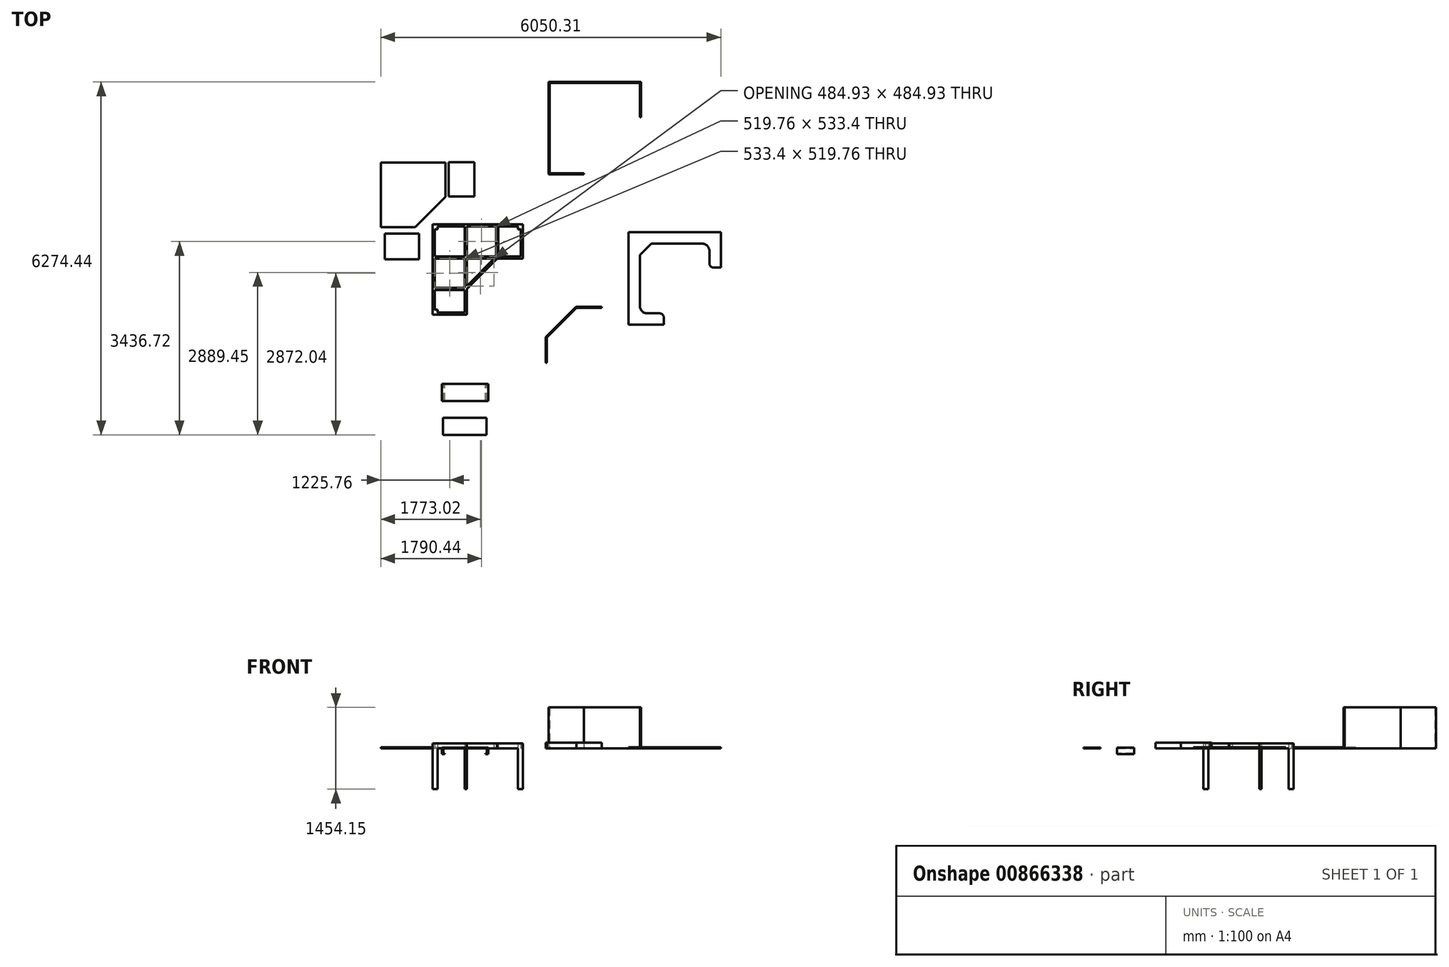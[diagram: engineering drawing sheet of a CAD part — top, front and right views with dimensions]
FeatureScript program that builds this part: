
annotation { "Feature Type Name" : "Feature", "Feature Type Description" : "" }
export const myFeature = defineFeature(function(context is Context, id is Id, definition is map)
    precondition{}
    {
        {
            var Q0;
            Q0=qCreatedBy(makeId("Top.planeOp"),FACE);
            var sketch = newSketch(context, id + "F0", { "sketchPlane" : qUnion([Q0])});
            skLineSegment(sketch, "E0.bottom", {"start": v(-1200.38, 871.33) * mm, "end": v(405.23, 871.33) * mm});
            skLineSegment(sketch, "E0.top", {"start": v(-1200.38, -734.28) * mm, "end": v(405.23, -734.28) * mm});
            skLineSegment(sketch, "E0.left", {"start": v(-1200.38, 871.33) * mm, "end": v(-1200.38, -734.28) * mm});
            skLineSegment(sketch, "E0.right", {"start": v(405.23, 871.33) * mm, "end": v(405.23, -734.28) * mm});
            skLineSegment(sketch, "E1.bottom", {"start": v(405.23, -734.28) * mm, "end": v(-590.78, -734.28) * mm});
            skLineSegment(sketch, "E1.top", {"start": v(405.23, 261.73) * mm, "end": v(-590.78, 261.73) * mm});
            skLineSegment(sketch, "E1.left", {"start": v(405.23, -734.28) * mm, "end": v(405.23, 261.73) * mm});
            skLineSegment(sketch, "E1.right", {"start": v(-590.78, -734.28) * mm, "end": v(-590.78, 261.73) * mm});
            skLineSegment(sketch, "E2", {"start": v(-590.78, -277.08) * mm, "end": v(-51.97, 261.73) * mm});
            skLineSegment(sketch, "E3", {"start": v(-590.78, -277.08) * mm, "end": v(-1200.38, -277.08) * mm});
            skLineSegment(sketch, "E4", {"start": v(-51.97, 261.73) * mm, "end": v(-51.97, 871.33) * mm});
            skLineSegment(sketch, "E5", {"start": v(-1200.38, -24.58) * mm, "end": v(-304.48, 871.33) * mm});
            skSolve(sketch);
        }
        {
            var Q0;
            {var subQ5=sQuery(id+"F0.wireOp",EDGE,"E3");Q0=makeQuery(id+"F0.imprint","IMPRINT",FACE,{"disambiguationData":[TD([[makeQuery(id+"F0.imprint","IMPRINT",EDGE,{"derivedFrom":subQ5}),-1.0]])]});}
            var Q1;
            {var subQ0=sQuery(id+"F0.wireOp",EDGE,"E2");Q1=makeQuery(id+"F0.imprint","IMPRINT",FACE,{"disambiguationData":[TD([[makeQuery(id+"F0.imprint","IMPRINT",EDGE,{"derivedFrom":subQ0}),1.0]])]});}
            var Q2;
            {var subQ3=sQuery(id+"F0.wireOp",EDGE,"E5");Q2=makeQuery(id+"F0.imprint","IMPRINT",FACE,{"disambiguationData":[TD([[makeQuery(id+"F0.imprint","IMPRINT",EDGE,{"derivedFrom":subQ3}),1.0]])]});}
            extrude(context, id + "F1", {"entities" : qUnion([Q0, Q1, Q2]), "depth" : 19.05 * mm, "offsetDistance" : 25.4 * mm});
        }
        {
            var Q0;
            Q0=qCreatedBy(makeId("Top.planeOp"),FACE);
            var sketch = newSketch(context, id + "F2", { "sketchPlane" : qUnion([Q0])});
            skLineSegment(sketch, "E6.bottom", {"start": v(-1128.15, -392.27) * mm, "end": v(-518.55, -392.27) * mm});
            skLineSegment(sketch, "E6.top", {"start": v(-1128.15, -849.47) * mm, "end": v(-518.55, -849.47) * mm});
            skLineSegment(sketch, "E6.left", {"start": v(-1128.15, -392.27) * mm, "end": v(-1128.15, -849.47) * mm});
            skLineSegment(sketch, "E6.right", {"start": v(-518.55, -392.27) * mm, "end": v(-518.55, -849.47) * mm});
            skLineSegment(sketch, "E7.bottom", {"start": v(3.93, 267.1) * mm, "end": v(461.13, 267.1) * mm});
            skLineSegment(sketch, "E7.top", {"start": v(3.93, 876.7) * mm, "end": v(461.13, 876.7) * mm});
            skLineSegment(sketch, "E7.left", {"start": v(3.93, 267.1) * mm, "end": v(3.93, 876.7) * mm});
            skLineSegment(sketch, "E7.right", {"start": v(461.13, 267.1) * mm, "end": v(461.13, 876.7) * mm});
            skSolve(sketch);
        }
        {
            var Q0;
            Q0=makeQuery(id+"F2.imprint","IMPRINT",FACE,{"disambiguationData":[TD([[makeQuery(id+"F2.imprint","IMPRINT",EDGE,{"derivedFrom":sQuery(id+"F2.wireOp",EDGE,"E6.bottom")}),-1.0]])]});
            var Q1;
            Q1=makeQuery(id+"F2.imprint","IMPRINT",FACE,{"disambiguationData":[TD([[makeQuery(id+"F2.imprint","IMPRINT",EDGE,{"derivedFrom":sQuery(id+"F2.wireOp",EDGE,"E7.bottom")}),1.0]])]});
            extrude(context, id + "F3", {"entities" : qUnion([Q0, Q1]), "depth" : 19.05 * mm, "offsetDistance" : 25.4 * mm});
        }
        {
            var Q0;
            Q0=qCreatedBy(makeId("Top.planeOp"),FACE);
            var sketch = newSketch(context, id + "F4", { "sketchPlane" : qUnion([Q0])});
            skLineSegment(sketch, "E8.bottom", {"start": v(-279.42, -229.72) * mm, "end": v(1326.19, -229.72) * mm});
            skLineSegment(sketch, "E8.top", {"start": v(-279.42, -1835.33) * mm, "end": v(1326.19, -1835.33) * mm});
            skLineSegment(sketch, "E8.left", {"start": v(-279.42, -229.72) * mm, "end": v(-279.42, -1835.33) * mm});
            skLineSegment(sketch, "E8.right", {"start": v(1326.19, -229.72) * mm, "end": v(1326.19, -1835.33) * mm});
            skLineSegment(sketch, "E9.bottom", {"start": v(1326.19, -1835.33) * mm, "end": v(330.18, -1835.33) * mm});
            skLineSegment(sketch, "E9.top", {"start": v(1326.19, -839.32) * mm, "end": v(330.18, -839.32) * mm});
            skLineSegment(sketch, "E9.left", {"start": v(1326.19, -1835.33) * mm, "end": v(1326.19, -839.32) * mm});
            skLineSegment(sketch, "E9.right", {"start": v(330.18, -1835.33) * mm, "end": v(330.18, -839.32) * mm});
            skLineSegment(sketch, "E10", {"start": v(330.18, -1378.13) * mm, "end": v(868.99, -839.32) * mm});
            skLineSegment(sketch, "E11.bottom", {"start": v(-279.42, -1746.43) * mm, "end": v(-241.32, -1746.43) * mm});
            skLineSegment(sketch, "E11.top", {"start": v(-279.42, -318.62) * mm, "end": v(-241.32, -318.62) * mm});
            skLineSegment(sketch, "E11.left", {"start": v(-279.42, -1746.43) * mm, "end": v(-279.42, -318.62) * mm});
            skLineSegment(sketch, "E11.right", {"start": v(-241.32, -1746.43) * mm, "end": v(-241.32, -318.62) * mm});
            skLineSegment(sketch, "E12.bottom", {"start": v(-190.52, -229.72) * mm, "end": v(1237.29, -229.72) * mm});
            skLineSegment(sketch, "E12.top", {"start": v(-190.52, -267.82) * mm, "end": v(1237.29, -267.82) * mm});
            skLineSegment(sketch, "E12.left", {"start": v(-190.52, -229.72) * mm, "end": v(-190.52, -267.82) * mm});
            skLineSegment(sketch, "E12.right", {"start": v(1237.29, -229.72) * mm, "end": v(1237.29, -267.82) * mm});
            skLineSegment(sketch, "E13.bottom", {"start": v(1326.19, -801.22) * mm, "end": v(1288.09, -801.22) * mm});
            skLineSegment(sketch, "E13.top", {"start": v(1326.19, -318.62) * mm, "end": v(1288.09, -318.62) * mm});
            skLineSegment(sketch, "E13.left", {"start": v(1326.19, -801.22) * mm, "end": v(1326.19, -318.62) * mm});
            skLineSegment(sketch, "E13.right", {"start": v(1288.09, -801.22) * mm, "end": v(1288.09, -318.62) * mm});
            skLineSegment(sketch, "E14.bottom", {"start": v(292.08, -1835.33) * mm, "end": v(-190.52, -1835.33) * mm});
            skLineSegment(sketch, "E14.top", {"start": v(292.08, -1797.23) * mm, "end": v(-190.52, -1797.23) * mm});
            skLineSegment(sketch, "E14.left", {"start": v(292.08, -1835.33) * mm, "end": v(292.08, -1797.23) * mm});
            skLineSegment(sketch, "E14.right", {"start": v(-190.52, -1835.33) * mm, "end": v(-190.52, -1797.23) * mm});
            skLineSegment(sketch, "E15.bottom", {"start": v(330.18, -1746.43) * mm, "end": v(292.08, -1746.43) * mm});
            skLineSegment(sketch, "E15.top", {"start": v(330.18, -267.82) * mm, "end": v(292.08, -267.82) * mm});
            skLineSegment(sketch, "E15.left", {"start": v(330.18, -1746.43) * mm, "end": v(330.18, -267.82) * mm});
            skLineSegment(sketch, "E15.right", {"start": v(292.08, -1746.43) * mm, "end": v(292.08, -267.82) * mm});
            skLineSegment(sketch, "E16.bottom", {"start": v(1237.29, -839.32) * mm, "end": v(-241.32, -839.32) * mm});
            skLineSegment(sketch, "E16.top", {"start": v(1237.29, -801.22) * mm, "end": v(-241.32, -801.22) * mm});
            skLineSegment(sketch, "E16.left", {"start": v(1237.29, -839.32) * mm, "end": v(1237.29, -801.22) * mm});
            skLineSegment(sketch, "E16.right", {"start": v(-241.32, -839.32) * mm, "end": v(-241.32, -801.22) * mm});
            skLineSegment(sketch, "E17.bottom", {"start": v(1326.19, -839.32) * mm, "end": v(1237.29, -839.32) * mm});
            skLineSegment(sketch, "E17.top", {"start": v(1326.19, -801.22) * mm, "end": v(1237.29, -801.22) * mm});
            skLineSegment(sketch, "E17.left", {"start": v(1326.19, -839.32) * mm, "end": v(1326.19, -801.22) * mm});
            skLineSegment(sketch, "E18.bottom", {"start": v(1326.19, -229.72) * mm, "end": v(1237.29, -229.72) * mm});
            skLineSegment(sketch, "E18.left", {"start": v(1326.19, -229.72) * mm, "end": v(1326.19, -318.61) * mm});
            skLineSegment(sketch, "E19.bottom", {"start": v(-279.42, -229.72) * mm, "end": v(-190.52, -229.72) * mm});
            skLineSegment(sketch, "E19.left", {"start": v(-279.42, -229.72) * mm, "end": v(-279.42, -318.61) * mm});
            skLineSegment(sketch, "E20.bottom", {"start": v(-279.42, -1835.33) * mm, "end": v(-190.52, -1835.33) * mm});
            skLineSegment(sketch, "E20.top", {"start": v(-279.42, -1746.43) * mm, "end": v(-190.52, -1746.43) * mm});
            skLineSegment(sketch, "E20.left", {"start": v(-279.42, -1835.33) * mm, "end": v(-279.42, -1746.43) * mm});
            skLineSegment(sketch, "E20.right", {"start": v(-190.52, -1835.33) * mm, "end": v(-190.52, -1746.43) * mm});
            skLineSegment(sketch, "E21.bottom", {"start": v(330.18, -1835.33) * mm, "end": v(292.08, -1835.33) * mm});
            skLineSegment(sketch, "E21.left", {"start": v(330.18, -1835.33) * mm, "end": v(330.18, -1746.43) * mm});
            skLineSegment(sketch, "E21.right", {"start": v(292.08, -1835.33) * mm, "end": v(292.08, -1746.43) * mm});
            skLineSegment(sketch, "E22", {"start": v(330.18, -1324.25) * mm, "end": v(815.1, -839.32) * mm});
            skLineSegment(sketch, "E23.bottom", {"start": v(888.04, -801.22) * mm, "end": v(849.94, -801.22) * mm});
            skLineSegment(sketch, "E23.top", {"start": v(888.04, -267.82) * mm, "end": v(849.94, -267.82) * mm});
            skLineSegment(sketch, "E23.left", {"start": v(888.04, -801.22) * mm, "end": v(888.04, -267.82) * mm});
            skLineSegment(sketch, "E23.right", {"start": v(849.94, -801.22) * mm, "end": v(849.94, -267.82) * mm});
            skLineSegment(sketch, "E24.bottom", {"start": v(292.08, -1397.18) * mm, "end": v(-241.32, -1397.18) * mm});
            skLineSegment(sketch, "E24.top", {"start": v(292.08, -1359.08) * mm, "end": v(-241.32, -1359.08) * mm});
            skLineSegment(sketch, "E24.left", {"start": v(292.08, -1397.18) * mm, "end": v(292.08, -1359.08) * mm});
            skLineSegment(sketch, "E24.right", {"start": v(-241.32, -1397.18) * mm, "end": v(-241.32, -1359.08) * mm});
            skLineSegment(sketch, "E25.top", {"start": v(1326.19, -318.62) * mm, "end": v(1237.29, -318.62) * mm});
            skLineSegment(sketch, "E25.left", {"start": v(1326.19, -229.72) * mm, "end": v(1326.19, -318.62) * mm});
            skLineSegment(sketch, "E25.right", {"start": v(1237.29, -229.72) * mm, "end": v(1237.29, -318.62) * mm});
            skLineSegment(sketch, "E26.top", {"start": v(-279.42, -318.62) * mm, "end": v(-190.52, -318.62) * mm});
            skLineSegment(sketch, "E26.left", {"start": v(-279.42, -229.72) * mm, "end": v(-279.42, -318.62) * mm});
            skLineSegment(sketch, "E26.right", {"start": v(-190.52, -229.72) * mm, "end": v(-190.52, -318.62) * mm});
            skSolve(sketch);
        }
        {
            var Q0;
            {var subQ6=sQuery(id+"F4.wireOp",EDGE,"E11.top");Q0=makeQuery(id+"F4.imprint","IMPRINT",FACE,{"disambiguationData":[TD([[makeQuery(id+"F4.imprint","IMPRINT",EDGE,{"derivedFrom":subQ6}),-1.0]])]});}
            var Q1;
            {var subQ1=sQuery(id+"F4.wireOp",EDGE,"E19.bottom");Q1=makeQuery(id+"F4.imprint","IMPRINT",FACE,{"disambiguationData":[TD([[makeQuery(id+"F4.imprint","IMPRINT",EDGE,{"derivedFrom":subQ1}),-1.0]])]});}
            var Q2;
            {var subQ3=sQuery(id+"F4.wireOp",EDGE,"E12.left");Q2=makeQuery(id+"F4.imprint","IMPRINT",FACE,{"disambiguationData":[TD([[makeQuery(id+"F4.imprint","IMPRINT",EDGE,{"derivedFrom":subQ3}),1.0]])]});}
            var Q3;
            {var subQ0=sQuery(id+"F4.wireOp",EDGE,"E15.left");var subQ1=sQuery(id+"F4.wireOp",EDGE,"E12.top");var subQ2=makeQuery(id+"F4.imprint","INTERSECT",VERTEX,{"derivedFrom":[subQ1,subQ0]});Q3=makeQuery(id+"F4.imprint","IMPRINT",FACE,{"disambiguationData":[TD([[makeQuery(id+"F4.imprint","IMPRINT",EDGE,{"disambiguationData":[TD([[subQ2,1.0]])],"derivedFrom":subQ1}),-1.0]])]});}
            var Q4;
            {var subQ0=sQuery(id+"F4.wireOp",EDGE,"E16.top");var subQ1=sQuery(id+"F4.wireOp",EDGE,"E11.right");var subQ2=makeQuery(id+"F4.imprint","INTERSECT",VERTEX,{"derivedFrom":[subQ1,subQ0]});Q4=makeQuery(id+"F4.imprint","IMPRINT",FACE,{"disambiguationData":[TD([[makeQuery(id+"F4.imprint","IMPRINT",EDGE,{"disambiguationData":[TD([[subQ2,1.0]])],"derivedFrom":subQ1}),-1.0]])]});}
            var Q5;
            {var subQ0=sQuery(id+"F4.wireOp",EDGE,"E16.top");var subQ5=sQuery(id+"F4.wireOp",EDGE,"E15.right");var subQ6=makeQuery(id+"F4.imprint","INTERSECT",VERTEX,{"derivedFrom":[subQ5,subQ0]});Q5=makeQuery(id+"F4.imprint","IMPRINT",FACE,{"disambiguationData":[TD([[makeQuery(id+"F4.imprint","IMPRINT",EDGE,{"disambiguationData":[TD([[subQ6,1.0]])],"derivedFrom":subQ5}),-1.0]])]});}
            var Q6;
            {var subQ3=sQuery(id+"F4.wireOp",EDGE,"E15.bottom");Q6=makeQuery(id+"F4.imprint","IMPRINT",FACE,{"disambiguationData":[TD([[makeQuery(id+"F4.imprint","IMPRINT",EDGE,{"derivedFrom":subQ3}),-1.0]])]});}
            var Q7;
            {var subQ7=sQuery(id+"F4.wireOp",EDGE,"E16.left");Q7=makeQuery(id+"F4.imprint","IMPRINT",FACE,{"disambiguationData":[TD([[makeQuery(id+"F4.imprint","IMPRINT",EDGE,{"derivedFrom":subQ7}),1.0]])]});}
            var Q8;
            {var subQ0=sQuery(id+"F4.wireOp",EDGE,"E23.left");Q8=makeQuery(id+"F4.imprint","IMPRINT",FACE,{"disambiguationData":[TD([[makeQuery(id+"F4.imprint","IMPRINT",EDGE,{"derivedFrom":subQ0}),1.0]])]});}
            var Q9;
            {var subQ1=sQuery(id+"F4.wireOp",EDGE,"E18.bottom");Q9=makeQuery(id+"F4.imprint","IMPRINT",FACE,{"disambiguationData":[TD([[makeQuery(id+"F4.imprint","IMPRINT",EDGE,{"derivedFrom":subQ1}),1.0]])]});}
            var Q10;
            Q10=makeQuery(id+"F4.imprint","IMPRINT",FACE,{"disambiguationData":[TD([[makeQuery(id+"F4.imprint","IMPRINT",EDGE,{"derivedFrom":sQuery(id+"F4.wireOp",EDGE,"E13.top")}),1.0]])]});
            var Q11;
            {var subQ4=sQuery(id+"F4.wireOp",EDGE,"E13.bottom");Q11=makeQuery(id+"F4.imprint","IMPRINT",FACE,{"disambiguationData":[TD([[makeQuery(id+"F4.imprint","IMPRINT",EDGE,{"derivedFrom":subQ4}),1.0]])]});}
            var Q12;
            {var subQ2=sQuery(id+"F4.wireOp",EDGE,"E24.bottom");Q12=makeQuery(id+"F4.imprint","IMPRINT",FACE,{"disambiguationData":[TD([[makeQuery(id+"F4.imprint","IMPRINT",EDGE,{"derivedFrom":subQ2}),-1.0]])]});}
            var Q13;
            {var subQ1=sQuery(id+"F4.wireOp",EDGE,"E11.bottom");Q13=makeQuery(id+"F4.imprint","IMPRINT",FACE,{"disambiguationData":[TD([[makeQuery(id+"F4.imprint","IMPRINT",EDGE,{"derivedFrom":subQ1}),-1.0]])]});}
            var Q14;
            Q14=makeQuery(id+"F4.imprint","IMPRINT",FACE,{"disambiguationData":[TD([[makeQuery(id+"F4.imprint","IMPRINT",EDGE,{"derivedFrom":sQuery(id+"F4.wireOp",EDGE,"E14.top")}),1.0]])]});
            var Q15;
            {var subQ4=sQuery(id+"F4.wireOp",EDGE,"E14.left");Q15=makeQuery(id+"F4.imprint","IMPRINT",FACE,{"disambiguationData":[TD([[makeQuery(id+"F4.imprint","IMPRINT",EDGE,{"derivedFrom":subQ4}),-1.0]])]});}
            var Q16;
            {var subQ2=sQuery(id+"F4.wireOp",EDGE,"E10");Q16=makeQuery(id+"F4.imprint","IMPRINT",FACE,{"disambiguationData":[TD([[makeQuery(id+"F4.imprint","IMPRINT",EDGE,{"derivedFrom":subQ2}),1.0]])]});}
            var Q17;
            {var subQ4=sQuery(id+"F4.wireOp",EDGE,"E11.bottom");Q17=makeQuery(id+"F4.imprint","IMPRINT",FACE,{"disambiguationData":[TD([[makeQuery(id+"F4.imprint","IMPRINT",EDGE,{"derivedFrom":subQ4}),1.0]])]});}
            var Q18;
            {var subQ1=sQuery(id+"F4.wireOp",EDGE,"E11.top");Q18=makeQuery(id+"F4.imprint","IMPRINT",FACE,{"disambiguationData":[TD([[makeQuery(id+"F4.imprint","IMPRINT",EDGE,{"derivedFrom":subQ1}),1.0]])]});}
            var Q19;
            {var subQ0=sQuery(id+"F4.wireOp",EDGE,"E12.right");Q19=makeQuery(id+"F4.imprint","IMPRINT",FACE,{"disambiguationData":[TD([[makeQuery(id+"F4.imprint","IMPRINT",EDGE,{"derivedFrom":subQ0}),1.0]])]});}
            var Q20;
            {var subQ2=sQuery(id+"F4.wireOp",EDGE,"E13.bottom");Q20=makeQuery(id+"F4.imprint","IMPRINT",FACE,{"disambiguationData":[TD([[makeQuery(id+"F4.imprint","IMPRINT",EDGE,{"derivedFrom":subQ2}),-1.0]])]});}
            extrude(context, id + "F5", {"entities" : qUnion([Q0, Q1, Q2, Q3, Q4, Q5, Q6, Q7, Q8, Q9, Q10, Q11, Q12, Q13, Q14, Q15, Q16, Q17, Q18, Q19, Q20]), "depth" : 88.9 * mm, "offsetDistance" : 25.4 * mm});
        }
        {
            var Q0;
            {var subQ1=sQuery(id+"F4.wireOp",EDGE,"E11.bottom");Q0=makeQuery(id+"F4.imprint","IMPRINT",FACE,{"disambiguationData":[TD([[makeQuery(id+"F4.imprint","IMPRINT",EDGE,{"derivedFrom":subQ1}),-1.0]])]});}
            var Q1;
            {var subQ4=sQuery(id+"F4.wireOp",EDGE,"E14.left");Q1=makeQuery(id+"F4.imprint","IMPRINT",FACE,{"disambiguationData":[TD([[makeQuery(id+"F4.imprint","IMPRINT",EDGE,{"derivedFrom":subQ4}),-1.0]])]});}
            var Q2;
            {var subQ1=sQuery(id+"F4.wireOp",EDGE,"E19.bottom");Q2=makeQuery(id+"F4.imprint","IMPRINT",FACE,{"disambiguationData":[TD([[makeQuery(id+"F4.imprint","IMPRINT",EDGE,{"derivedFrom":subQ1}),-1.0]])]});}
            var Q3;
            {var subQ1=sQuery(id+"F4.wireOp",EDGE,"E18.bottom");Q3=makeQuery(id+"F4.imprint","IMPRINT",FACE,{"disambiguationData":[TD([[makeQuery(id+"F4.imprint","IMPRINT",EDGE,{"derivedFrom":subQ1}),1.0]])]});}
            var Q4;
            {var subQ4=sQuery(id+"F4.wireOp",EDGE,"E13.bottom");Q4=makeQuery(id+"F4.imprint","IMPRINT",FACE,{"disambiguationData":[TD([[makeQuery(id+"F4.imprint","IMPRINT",EDGE,{"derivedFrom":subQ4}),1.0]])]});}
            var Q5;
            {var subQ0=sQuery(id+"F4.wireOp",EDGE,"E12.right");Q5=makeQuery(id+"F4.imprint","IMPRINT",FACE,{"disambiguationData":[TD([[makeQuery(id+"F4.imprint","IMPRINT",EDGE,{"derivedFrom":subQ0}),1.0]])]});}
            var Q6;
            {var subQ1=sQuery(id+"F4.wireOp",EDGE,"E11.top");Q6=makeQuery(id+"F4.imprint","IMPRINT",FACE,{"disambiguationData":[TD([[makeQuery(id+"F4.imprint","IMPRINT",EDGE,{"derivedFrom":subQ1}),1.0]])]});}
            extrude(context, id + "F6", {"entities" : qUnion([Q0, Q1, Q2, Q3, Q4, Q5, Q6]), "operationType" : NewBodyOperationType.ADD, "oppositeDirection" : true, "depth" : 723.9 * mm, "offsetDistance" : 25.4 * mm});
        }
        {
            var Q0;
            Q0=qCreatedBy(makeId("Top.planeOp"),FACE);
            var sketch = newSketch(context, id + "F7", { "sketchPlane" : qUnion([Q0])});
            skLineSegment(sketch, "E27.bottom", {"start": v(1782.3, 659.5) * mm, "end": v(3426.02, 659.5) * mm});
            skLineSegment(sketch, "E27.top", {"start": v(1782.3, 2303.2) * mm, "end": v(3426.02, 2303.2) * mm});
            skLineSegment(sketch, "E27.left", {"start": v(1782.3, 659.5) * mm, "end": v(1782.3, 2303.2) * mm});
            skLineSegment(sketch, "E27.right", {"start": v(3426.02, 659.5) * mm, "end": v(3426.02, 2303.2) * mm});
            skLineSegment(sketch, "E28.bottom", {"start": v(3406.97, 678.54) * mm, "end": v(1801.36, 678.54) * mm});
            skLineSegment(sketch, "E28.top", {"start": v(3406.97, 2284.15) * mm, "end": v(1801.36, 2284.15) * mm});
            skLineSegment(sketch, "E28.left", {"start": v(3406.97, 678.54) * mm, "end": v(3406.97, 2284.15) * mm});
            skLineSegment(sketch, "E28.right", {"start": v(1801.36, 678.54) * mm, "end": v(1801.36, 2284.15) * mm});
            skLineSegment(sketch, "E29.bottom", {"start": v(3406.97, 1674.55) * mm, "end": v(3426.02, 1674.55) * mm});
            skLineSegment(sketch, "E29.top", {"start": v(3406.97, 659.5) * mm, "end": v(3426.02, 659.5) * mm});
            skLineSegment(sketch, "E29.left", {"start": v(3406.97, 1674.55) * mm, "end": v(3406.97, 659.5) * mm});
            skLineSegment(sketch, "E29.right", {"start": v(3426.02, 1674.55) * mm, "end": v(3426.02, 659.5) * mm});
            skLineSegment(sketch, "E30.bottom", {"start": v(2410.96, 678.54) * mm, "end": v(3406.97, 678.54) * mm});
            skLineSegment(sketch, "E30.top", {"start": v(2410.96, 659.5) * mm, "end": v(3406.97, 659.5) * mm});
            skLineSegment(sketch, "E30.left", {"start": v(2410.96, 678.54) * mm, "end": v(2410.96, 659.5) * mm});
            skLineSegment(sketch, "E30.right", {"start": v(3406.97, 678.54) * mm, "end": v(3406.97, 659.5) * mm});
            skSolve(sketch);
        }
        {
            var Q0;
            {var subQ2=sQuery(id+"F7.wireOp",EDGE,"E27.top");Q0=makeQuery(id+"F7.imprint","IMPRINT",FACE,{"disambiguationData":[TD([[makeQuery(id+"F7.imprint","IMPRINT",EDGE,{"derivedFrom":subQ2}),-1.0]])]});}
            extrude(context, id + "F8", {"entities" : qUnion([Q0]), "depth" : 730.25 * mm, "offsetDistance" : 25.4 * mm});
        }
        {
            var Q0;
            Q0=qCreatedBy(makeId("Top.planeOp"),FACE);
            var sketch = newSketch(context, id + "F9", { "sketchPlane" : qUnion([Q0])});
            skLineSegment(sketch, "E31.bottom", {"start": v(3206.22, -369.75) * mm, "end": v(4849.93, -369.75) * mm});
            skLineSegment(sketch, "E31.top", {"start": v(3206.22, -2013.46) * mm, "end": v(4849.93, -2013.46) * mm});
            skLineSegment(sketch, "E31.left", {"start": v(3206.22, -369.75) * mm, "end": v(3206.22, -2013.46) * mm});
            skLineSegment(sketch, "E31.right", {"start": v(4849.93, -369.75) * mm, "end": v(4849.93, -2013.46) * mm});
            skLineSegment(sketch, "E32.bottom", {"start": v(4849.93, -2013.46) * mm, "end": v(3409.42, -2013.46) * mm});
            skLineSegment(sketch, "E32.top", {"start": v(4519.73, -572.95) * mm, "end": v(3409.42, -572.95) * mm});
            skLineSegment(sketch, "E32.left", {"start": v(4849.93, -2013.46) * mm, "end": v(4849.93, -572.95) * mm});
            skLineSegment(sketch, "E32.right", {"start": v(3409.42, -1683.26) * mm, "end": v(3409.42, -572.95) * mm});
            skLineSegment(sketch, "E33.bottom", {"start": v(4849.93, -998.4) * mm, "end": v(4722.93, -998.4) * mm});
            skLineSegment(sketch, "E33.top", {"start": v(4849.93, -572.95) * mm, "end": v(4608.63, -572.95) * mm});
            skLineSegment(sketch, "E33.left", {"start": v(4849.93, -998.4) * mm, "end": v(4849.93, -572.95) * mm});
            skLineSegment(sketch, "E33.right", {"start": v(4646.73, -922.2) * mm, "end": v(4646.73, -699.95) * mm});
            skLineSegment(sketch, "E34.bottom", {"start": v(3834.87, -2013.46) * mm, "end": v(3409.42, -2013.46) * mm});
            skLineSegment(sketch, "E34.top", {"start": v(3758.67, -1810.26) * mm, "end": v(3536.42, -1810.26) * mm});
            skLineSegment(sketch, "E34.left", {"start": v(3834.87, -2013.46) * mm, "end": v(3834.87, -1886.46) * mm});
            skLineSegment(sketch, "E34.right", {"start": v(3409.42, -2013.46) * mm, "end": v(3409.42, -1810.26) * mm});
            skLineSegment(sketch, "E35", {"start": v(3409.42, -776.15) * mm, "end": v(3612.62, -572.95) * mm});
            skPoint(sketch, "E36.visualSharp", {"position": v(4646.73, -998.4) * mm});
            skArc(sketch, "E36.filletArc", {"start": v(4646.73, -922.2) * mm, "mid": v(4669.05, -976.09) * mm, "end": v(4722.93, -998.4) * mm});
            skArc(sketch, "E37.filletArc", {"start": v(4646.73, -699.95) * mm, "mid": v(4609.53, -610.15) * mm, "end": v(4519.73, -572.95) * mm});
            skPoint(sketch, "E38.visualSharp", {"position": v(3834.87, -1810.26) * mm});
            skArc(sketch, "E38.filletArc", {"start": v(3834.87, -1886.46) * mm, "mid": v(3812.55, -1832.58) * mm, "end": v(3758.67, -1810.26) * mm});
            skArc(sketch, "E39.filletArc", {"start": v(3409.42, -1683.26) * mm, "mid": v(3446.62, -1773.07) * mm, "end": v(3536.42, -1810.26) * mm});
            skSolve(sketch);
        }
        {
            var Q0;
            {var subQ9=sQuery(id+"F9.wireOp",EDGE,"E31.bottom");Q0=makeQuery(id+"F9.imprint","IMPRINT",FACE,{"disambiguationData":[TD([[makeQuery(id+"F9.imprint","IMPRINT",EDGE,{"derivedFrom":subQ9}),-1.0]])]});}
            var Q1;
            {var subQ3=sQuery(id+"F9.wireOp",EDGE,"E35");Q1=makeQuery(id+"F9.imprint","IMPRINT",FACE,{"disambiguationData":[TD([[makeQuery(id+"F9.imprint","IMPRINT",EDGE,{"derivedFrom":subQ3}),1.0]])]});}
            extrude(context, id + "F10", {"entities" : qUnion([Q0, Q1]), "depth" : 19.05 * mm, "offsetDistance" : 25.4 * mm});
        }
        {
            var Q0;
            Q0=qCreatedBy(makeId("Top.planeOp"),FACE);
            var sketch = newSketch(context, id + "F11", { "sketchPlane" : qUnion([Q0])});
            skLineSegment(sketch, "E40.bottom", {"start": v(2729.17, -2688.31) * mm, "end": v(1733.16, -2688.31) * mm});
            skLineSegment(sketch, "E40.top", {"start": v(2729.17, -1692.3) * mm, "end": v(1733.16, -1692.3) * mm});
            skLineSegment(sketch, "E40.left", {"start": v(2729.17, -2688.31) * mm, "end": v(2729.17, -1692.3) * mm});
            skLineSegment(sketch, "E40.right", {"start": v(1733.16, -2688.31) * mm, "end": v(1733.16, -1692.3) * mm});
            skLineSegment(sketch, "E41", {"start": v(1733.16, -2231.11) * mm, "end": v(2271.97, -1692.3) * mm});
            skLineSegment(sketch, "E42", {"start": v(1733.16, -2258.05) * mm, "end": v(2298.91, -1692.3) * mm});
            skLineSegment(sketch, "E43.bottom", {"start": v(2729.17, -2688.31) * mm, "end": v(1752.21, -2688.31) * mm});
            skLineSegment(sketch, "E43.top", {"start": v(2729.17, -1711.35) * mm, "end": v(1752.21, -1711.35) * mm});
            skLineSegment(sketch, "E43.left", {"start": v(2729.17, -2688.31) * mm, "end": v(2729.17, -1711.35) * mm});
            skLineSegment(sketch, "E43.right", {"start": v(1752.21, -2688.31) * mm, "end": v(1752.21, -1711.35) * mm});
            skSolve(sketch);
        }
        {
            var Q0;
            {var subQ0=sQuery(id+"F11.wireOp",EDGE,"E41");var subQ1=sQuery(id+"F11.wireOp",EDGE,"E40.right");var subQ2=makeQuery(id+"F11.imprint","INTERSECT",VERTEX,{"derivedFrom":[subQ1,subQ0]});Q0=makeQuery(id+"F11.imprint","IMPRINT",FACE,{"disambiguationData":[TD([[makeQuery(id+"F11.imprint","IMPRINT",EDGE,{"disambiguationData":[TD([[subQ2,1.0]])],"derivedFrom":subQ1}),-1.0]])]});}
            var Q1;
            {var subQ0=sQuery(id+"F11.wireOp",EDGE,"E40.right");var subQ1=sQuery(id+"F11.wireOp",EDGE,"E40.bottom");var subQ2=makeQuery(id+"F11.imprint","INTERSECT",VERTEX,{"derivedFrom":[subQ1,subQ0]});Q1=makeQuery(id+"F11.imprint","IMPRINT",FACE,{"disambiguationData":[TD([[makeQuery(id+"F11.imprint","IMPRINT",EDGE,{"disambiguationData":[TD([[subQ2,1.0]])],"derivedFrom":subQ1}),-1.0]])]});}
            var Q2;
            {var subQ0=sQuery(id+"F11.wireOp",EDGE,"E43.right");var subQ1=sQuery(id+"F11.wireOp",EDGE,"E41");var subQ2=makeQuery(id+"F11.imprint","INTERSECT",VERTEX,{"derivedFrom":[subQ1,subQ0]});Q2=makeQuery(id+"F11.imprint","IMPRINT",FACE,{"disambiguationData":[TD([[makeQuery(id+"F11.imprint","IMPRINT",EDGE,{"disambiguationData":[TD([[subQ2,-1.0]])],"derivedFrom":subQ1}),-1.0]])]});}
            var Q3;
            {var subQ0=sQuery(id+"F11.wireOp",EDGE,"E41");var subQ1=sQuery(id+"F11.wireOp",EDGE,"E40.top");var subQ2=makeQuery(id+"F11.imprint","INTERSECT",VERTEX,{"derivedFrom":[subQ1,subQ0]});Q3=makeQuery(id+"F11.imprint","IMPRINT",FACE,{"disambiguationData":[TD([[makeQuery(id+"F11.imprint","IMPRINT",EDGE,{"disambiguationData":[TD([[subQ2,1.0]])],"derivedFrom":subQ1}),1.0]])]});}
            var Q4;
            {var subQ0=sQuery(id+"F11.wireOp",EDGE,"E40.left");var subQ1=sQuery(id+"F11.wireOp",EDGE,"E40.top");var subQ2=makeQuery(id+"F11.imprint","INTERSECT",VERTEX,{"derivedFrom":[subQ1,subQ0]});Q4=makeQuery(id+"F11.imprint","IMPRINT",FACE,{"disambiguationData":[TD([[makeQuery(id+"F11.imprint","IMPRINT",EDGE,{"disambiguationData":[TD([[subQ2,-1.0]])],"derivedFrom":subQ1}),1.0]])]});}
            extrude(context, id + "F12", {"entities" : qUnion([Q0, Q1, Q2, Q3, Q4]), "depth" : 101.6 * mm, "offsetDistance" : 25.4 * mm});
        }
        {
            var Q0;
            Q0=qCreatedBy(makeId("Top.planeOp"),FACE);
            var sketch = newSketch(context, id + "F13", { "sketchPlane" : qUnion([Q0])});
            skLineSegment(sketch, "E44.bottom", {"start": v(-96.34, -3666.44) * mm, "end": v(678.36, -3666.44) * mm});
            skLineSegment(sketch, "E44.top", {"start": v(-96.34, -3971.24) * mm, "end": v(678.36, -3971.24) * mm});
            skLineSegment(sketch, "E44.left", {"start": v(-96.34, -3666.44) * mm, "end": v(-96.34, -3971.24) * mm});
            skLineSegment(sketch, "E44.right", {"start": v(678.36, -3666.44) * mm, "end": v(678.36, -3971.24) * mm});
            skLineSegment(sketch, "E45.bottom", {"start": v(-114.3, -3372.04) * mm, "end": v(711.2, -3372.04) * mm});
            skLineSegment(sketch, "E45.top", {"start": v(-114.3, -3067.24) * mm, "end": v(711.2, -3067.24) * mm});
            skLineSegment(sketch, "E45.left", {"start": v(-114.3, -3372.04) * mm, "end": v(-114.3, -3067.24) * mm});
            skLineSegment(sketch, "E45.right", {"start": v(711.2, -3372.04) * mm, "end": v(711.2, -3067.24) * mm});
            skSolve(sketch);
        }
        {
            var Q0;
            Q0=makeQuery(id+"F13.imprint","IMPRINT",FACE,{"disambiguationData":[TD([[makeQuery(id+"F13.imprint","IMPRINT",EDGE,{"derivedFrom":sQuery(id+"F13.wireOp",EDGE,"E45.bottom")}),1.0]])]});
            var Q1;
            Q1=makeQuery(id+"F13.imprint","IMPRINT",FACE,{"disambiguationData":[TD([[makeQuery(id+"F13.imprint","IMPRINT",EDGE,{"derivedFrom":sQuery(id+"F13.wireOp",EDGE,"E44.bottom")}),-1.0]])]});
            extrude(context, id + "F14", {"entities" : qUnion([Q0, Q1]), "depth" : 12.7 * mm, "offsetDistance" : 25.4 * mm});
        }
        {
            var Q0;
            Q0=makeQuery(id+"F14.opExtrude","CAP_FACE",FACE,{"disambiguationData":[OSD([sQuery(id+"F13.wireOp",EDGE,"E45.bottom"),sQuery(id+"F13.wireOp",EDGE,"E45.top"),sQuery(id+"F13.wireOp",EDGE,"E45.left"),sQuery(id+"F13.wireOp",EDGE,"E45.right")])],"isStart":true});
            var sketch = newSketch(context, id + "F15", { "sketchPlane" : qUnion([Q0])});
            skLineSegment(sketch, "E46.bottom", {"start": v(-88.9, 3372.04) * mm, "end": v(685.8, 3372.04) * mm});
            skLineSegment(sketch, "E46.top", {"start": v(-88.9, 3067.24) * mm, "end": v(685.8, 3067.24) * mm});
            skLineSegment(sketch, "E46.left", {"start": v(-88.9, 3372.04) * mm, "end": v(-88.9, 3067.24) * mm});
            skLineSegment(sketch, "E46.right", {"start": v(685.8, 3372.04) * mm, "end": v(685.8, 3067.24) * mm});
            skSolve(sketch);
        }
        {
            var Q0;
            {var subQ0=sQuery(id+"F15.wireOp",EDGE,"E46.left");Q0=makeQuery(id+"F15.imprint","IMPRINT",FACE,{"disambiguationData":[TD([[makeQuery(id+"F15.imprint","IMPRINT",EDGE,{"derivedFrom":subQ0}),-1.0]])]});}
            var Q1;
            {var subQ0=sQuery(id+"F15.wireOp",EDGE,"E46.right");Q1=makeQuery(id+"F15.imprint","IMPRINT",FACE,{"disambiguationData":[TD([[makeQuery(id+"F15.imprint","IMPRINT",EDGE,{"derivedFrom":subQ0}),1.0]])]});}
            extrude(context, id + "F16", {"entities" : qUnion([Q0, Q1]), "operationType" : NewBodyOperationType.ADD, "depth" : 101.6 * mm, "offsetDistance" : 25.4 * mm});
        }
        {
            var Q0;
            Q0=makeQuery(id+"F16.opExtrude","SWEPT_FACE",FACE,{"disambiguationData":[OSD([sQuery(id+"F15.wireOp",EDGE,"E46.left")])]});
            var sketch = newSketch(context, id + "F17", { "sketchPlane" : qUnion([Q0])});
            skLineSegment(sketch, "E47.bottom", {"start": v(-3067.24, -101.6) * mm, "end": v(-3372.04, -101.6) * mm});
            skLineSegment(sketch, "E47.top", {"start": v(-3067.24, -88.9) * mm, "end": v(-3372.04, -88.9) * mm});
            skLineSegment(sketch, "E47.left", {"start": v(-3067.24, -101.6) * mm, "end": v(-3067.24, -88.9) * mm});
            skLineSegment(sketch, "E47.right", {"start": v(-3372.04, -101.6) * mm, "end": v(-3372.04, -88.9) * mm});
            skSolve(sketch);
        }
        {
            var Q0;
            Q0=makeQuery(id+"F17.imprint","IMPRINT",FACE,{"disambiguationData":[TD([[makeQuery(id+"F17.imprint","IMPRINT",EDGE,{"derivedFrom":sQuery(id+"F17.wireOp",EDGE,"E47.bottom")}),1.0]])]});
            extrude(context, id + "F18", {"entities" : qUnion([Q0]), "operationType" : NewBodyOperationType.ADD, "depth" : 25.4 * mm, "offsetDistance" : 25.4 * mm});
        }
        {
            var Q0;
            Q0=makeQuery(id+"F16.opExtrude","SWEPT_FACE",FACE,{"disambiguationData":[OSD([sQuery(id+"F15.wireOp",EDGE,"E46.right")])]});
            var sketch = newSketch(context, id + "F19", { "sketchPlane" : qUnion([Q0])});
            skLineSegment(sketch, "E48.bottom", {"start": v(3067.24, -101.6) * mm, "end": v(3372.04, -101.6) * mm});
            skLineSegment(sketch, "E48.top", {"start": v(3067.24, -88.9) * mm, "end": v(3372.04, -88.9) * mm});
            skLineSegment(sketch, "E48.left", {"start": v(3067.24, -101.6) * mm, "end": v(3067.24, -88.9) * mm});
            skLineSegment(sketch, "E48.right", {"start": v(3372.04, -101.6) * mm, "end": v(3372.04, -88.9) * mm});
            skSolve(sketch);
        }
        {
            var Q0;
            Q0=makeQuery(id+"F19.imprint","IMPRINT",FACE,{"disambiguationData":[TD([[makeQuery(id+"F19.imprint","IMPRINT",EDGE,{"derivedFrom":sQuery(id+"F19.wireOp",EDGE,"E48.bottom")}),-1.0]])]});
            extrude(context, id + "F20", {"entities" : qUnion([Q0]), "operationType" : NewBodyOperationType.ADD, "depth" : 25.4 * mm, "offsetDistance" : 25.4 * mm});
        }
    });
